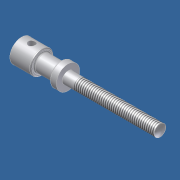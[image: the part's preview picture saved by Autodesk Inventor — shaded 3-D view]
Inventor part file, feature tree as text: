
AUTODESK INVENTOR PART (.ipt)
format: ipt  version: unknown  size: 222,720 bytes
history: native  units: in
note: dims shown in document units (in); Inventor stores cm internally (conversion verified against a paired STEP export)
features: plane x2, fillet x2, sketch x2, revolve x1, hole x1, thread x1
ambient origin geometry x8: Origin, YZ Plane, XZ Plane, XY Plane, X Axis, Y Axis, Z Axis, Center Point
bodies: Solid1 (feature_tree)
feature tree (9):
  revolve  "Revolution1"  [1 undecoded]
  plane  "Work Plane2"
  hole  "Hole1"  [1 undecoded]
  fillet  "Fillet1"  Radius=3.813in
  fillet  "Fillet2"  Radius=0.219in
  thread  "Thread5"  [1 undecoded]
  sketch  "Sketch1"  dims[d0=2.5in d1=0.188in]
  plane  "Work Plane1"
  sketch  "Sketch2"  dims[d4=0.1562in d5=0.3125in d7=3.813in d8=0.219in d9=0.032in d11=0.625in d12=0.063in d13=2.5in d14=0.3125in d15=90.0deg d24=0.28in d25=0.185in d26=0.75in d27=0.375in d28=0.25in d29=0.5635in d30=1.0in d31=0.8108in d32=0.0313in d33=0.0313in d34=2.219in d35=0.313in]
note: 3 required parameter values undecoded (feature->parameter linkage not recoverable at this tier; creation-order binding heuristic only, values carry confidence <= 0.55)